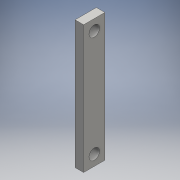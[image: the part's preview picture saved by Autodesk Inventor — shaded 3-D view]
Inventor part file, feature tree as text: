
AUTODESK INVENTOR PART (.ipt)
format: ipt  version: 2016 (Build 200138000, 138)  size: 114,176 bytes
history: native  units: mm
features: extrude x4, sketch x3, other x2
ambient origin geometry x8: Origin, YZ Plane, XZ Plane, XY Plane, X Axis, Y Axis, Z Axis, Center Point
bodies: Body1 (feature_tree)
feature tree (9):
  other  "ソリッド1"
  extrude  "押し出し1"  Depth=30.0mm
  extrude  "押し出し2"  Depth=5.0mm TaperAngle=0.0deg
  extrude  "押し出し4"  Depth=2.0mm
  other  "作業平面1"
  extrude  "押し出し5"  Depth=10.0mm
  sketch  "スケッチ2"
  sketch  "スケッチ4"
  sketch  "スケッチ5"
